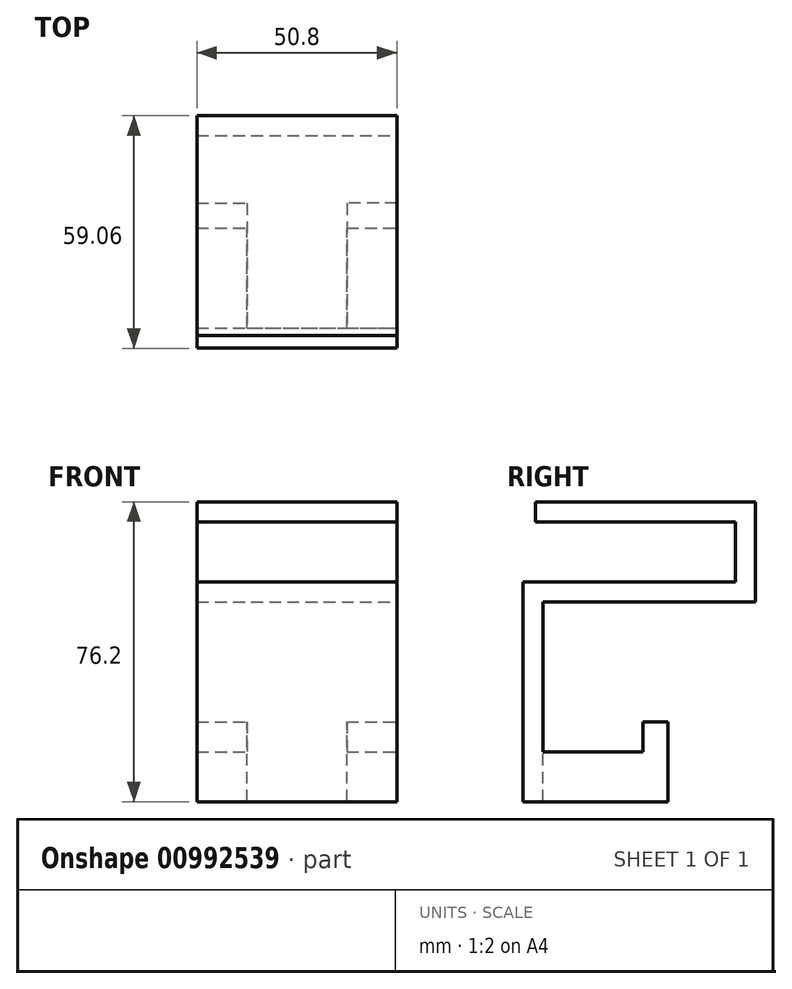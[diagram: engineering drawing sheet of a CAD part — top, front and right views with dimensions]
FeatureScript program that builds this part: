
annotation { "Feature Type Name" : "Feature", "Feature Type Description" : "" }
export const myFeature = defineFeature(function(context is Context, id is Id, definition is map)
    precondition{}
    {
        {
            var Q0;
            Q0=qCreatedBy(makeId("Top.planeOp"),FACE);
            var sketch = newSketch(context, id + "F0", { "sketchPlane" : qUnion([Q0])});
            skLineSegment(sketch, "E0.bottom", {"start": v(0, 0) * mm, "end": v(50.8, 0) * mm});
            skLineSegment(sketch, "E0.top", {"start": v(0, 55.88) * mm, "end": v(50.8, 55.88) * mm});
            skLineSegment(sketch, "E0.left", {"start": v(0, 0) * mm, "end": v(0, 55.88) * mm});
            skLineSegment(sketch, "E0.right", {"start": v(50.8, 0) * mm, "end": v(50.8, 55.88) * mm});
            skSolve(sketch);
        }
        {
            var Q0;
            Q0=makeQuery(id+"F0.imprint","IMPRINT",FACE,{"disambiguationData":[TD([[makeQuery(id+"F0.imprint","IMPRINT",EDGE,{"derivedFrom":sQuery(id+"F0.wireOp",EDGE,"E0.bottom")}),1.0]])]});
            extrude(context, id + "F1", {"entities" : qUnion([Q0]), "depth" : 5.08 * mm, "offsetDistance" : 25.4 * mm});
        }
        {
            var Q0;
            Q0=makeQuery(id+"F1.opExtrude","CAP_FACE",FACE,{"disambiguationData":[OSD([sQuery(id+"F0.wireOp",EDGE,"E0.bottom"),sQuery(id+"F0.wireOp",EDGE,"E0.top"),sQuery(id+"F0.wireOp",EDGE,"E0.left"),sQuery(id+"F0.wireOp",EDGE,"E0.right")])],"isStart":true});
            var sketch = newSketch(context, id + "F2", { "sketchPlane" : qUnion([Q0])});
            skLineSegment(sketch, "E1.bottom", {"start": v(0, -55.88) * mm, "end": v(50.8, -55.88) * mm});
            skLineSegment(sketch, "E1.top", {"start": v(0, -50.8) * mm, "end": v(50.8, -50.8) * mm});
            skLineSegment(sketch, "E1.left", {"start": v(0, -55.88) * mm, "end": v(0, -50.8) * mm});
            skLineSegment(sketch, "E1.right", {"start": v(50.8, -55.88) * mm, "end": v(50.8, -50.8) * mm});
            skSolve(sketch);
        }
        {
            var Q0;
            Q0=makeQuery(id+"F2.imprint","IMPRINT",FACE,{"disambiguationData":[TD([[makeQuery(id+"F2.imprint","IMPRINT",EDGE,{"derivedFrom":sQuery(id+"F2.wireOp",EDGE,"E1.bottom")}),1.0]])]});
            extrude(context, id + "F3", {"entities" : qUnion([Q0]), "operationType" : NewBodyOperationType.ADD, "depth" : 20.32 * mm, "offsetDistance" : 25.4 * mm});
        }
        {
            var Q0;
            Q0=makeQuery(id+"F3.opExtrude","SWEPT_FACE",FACE,{"disambiguationData":[OSD([sQuery(id+"F2.wireOp",EDGE,"E1.top")])]});
            var sketch = newSketch(context, id + "F4", { "sketchPlane" : qUnion([Q0])});
            skLineSegment(sketch, "E2.bottom", {"start": v(0, -20.32) * mm, "end": v(50.8, -20.32) * mm});
            skLineSegment(sketch, "E2.top", {"start": v(0, -15.24) * mm, "end": v(50.8, -15.24) * mm});
            skLineSegment(sketch, "E2.left", {"start": v(0, -20.32) * mm, "end": v(0, -15.24) * mm});
            skLineSegment(sketch, "E2.right", {"start": v(50.8, -20.32) * mm, "end": v(50.8, -15.24) * mm});
            skSolve(sketch);
        }
        {
            var Q0;
            Q0=makeQuery(id+"F4.imprint","IMPRINT",FACE,{"disambiguationData":[TD([[makeQuery(id+"F4.imprint","IMPRINT",EDGE,{"derivedFrom":sQuery(id+"F4.wireOp",EDGE,"E2.bottom")}),1.0]])]});
            extrude(context, id + "F5", {"entities" : qUnion([Q0]), "operationType" : NewBodyOperationType.ADD, "depth" : 53.97 * mm, "offsetDistance" : 25.4 * mm});
        }
        {
            var Q0;
            Q0=makeQuery(id+"F5.boolean.opBoolean","MERGE",FACE,{"derivedFrom":[makeQuery(id+"F3.opExtrude","CAP_FACE",FACE,{"disambiguationData":[OSD([sQuery(id+"F2.wireOp",EDGE,"E1.bottom"),sQuery(id+"F2.wireOp",EDGE,"E1.top"),sQuery(id+"F2.wireOp",EDGE,"E1.left"),sQuery(id+"F2.wireOp",EDGE,"E1.right")])],"isStart":false}),makeQuery(id+"F5.opExtrude","SWEPT_FACE",FACE,{"disambiguationData":[OSD([sQuery(id+"F4.wireOp",EDGE,"E2.bottom")])]})]});
            var sketch = newSketch(context, id + "F6", { "sketchPlane" : qUnion([Q0])});
            skLineSegment(sketch, "E3.bottom", {"start": v(0, 3.17) * mm, "end": v(50.8, 3.17) * mm});
            skLineSegment(sketch, "E3.top", {"start": v(0, -1.9) * mm, "end": v(50.8, -1.9) * mm});
            skLineSegment(sketch, "E3.left", {"start": v(0, 3.17) * mm, "end": v(0, -1.9) * mm});
            skLineSegment(sketch, "E3.right", {"start": v(50.8, 3.17) * mm, "end": v(50.8, -1.9) * mm});
            skSolve(sketch);
        }
        {
            var Q0;
            Q0=makeQuery(id+"F6.imprint","IMPRINT",FACE,{"disambiguationData":[TD([[makeQuery(id+"F6.imprint","IMPRINT",EDGE,{"derivedFrom":sQuery(id+"F6.wireOp",EDGE,"E3.bottom")}),-1.0]])]});
            extrude(context, id + "F7", {"entities" : qUnion([Q0]), "operationType" : NewBodyOperationType.ADD, "depth" : 50.8 * mm, "offsetDistance" : 25.4 * mm});
        }
        {
            var Q0;
            Q0=makeQuery(id+"F7.opExtrude","SWEPT_FACE",FACE,{"disambiguationData":[OSD([sQuery(id+"F6.wireOp",EDGE,"E3.top")])]});
            var sketch = newSketch(context, id + "F8", { "sketchPlane" : qUnion([Q0])});
            skLineSegment(sketch, "E4.bottom", {"start": v(-50.8, -71.12) * mm, "end": v(-38.1, -71.12) * mm});
            skLineSegment(sketch, "E4.top", {"start": v(-50.8, -50.8) * mm, "end": v(-38.1, -50.8) * mm});
            skLineSegment(sketch, "E4.left", {"start": v(-50.8, -71.12) * mm, "end": v(-50.8, -50.8) * mm});
            skLineSegment(sketch, "E4.right", {"start": v(-38.1, -71.12) * mm, "end": v(-38.1, -50.8) * mm});
            skLineSegment(sketch, "E5.bottom", {"start": v(0, -71.12) * mm, "end": v(-12.7, -71.12) * mm});
            skLineSegment(sketch, "E5.top", {"start": v(0, -50.8) * mm, "end": v(-12.7, -50.8) * mm});
            skLineSegment(sketch, "E5.left", {"start": v(0, -71.12) * mm, "end": v(0, -50.8) * mm});
            skLineSegment(sketch, "E5.right", {"start": v(-12.7, -71.12) * mm, "end": v(-12.7, -50.8) * mm});
            skSolve(sketch);
        }
        {
            var Q0;
            Q0=makeQuery(id+"F8.imprint","IMPRINT",FACE,{"disambiguationData":[TD([[makeQuery(id+"F8.imprint","IMPRINT",EDGE,{"derivedFrom":sQuery(id+"F8.wireOp",EDGE,"E4.bottom")}),-1.0]])]});
            var Q1;
            Q1=makeQuery(id+"F8.imprint","IMPRINT",FACE,{"disambiguationData":[TD([[makeQuery(id+"F8.imprint","IMPRINT",EDGE,{"derivedFrom":sQuery(id+"F8.wireOp",EDGE,"E5.bottom")}),-1.0]])]});
            extrude(context, id + "F9", {"entities" : qUnion([Q0, Q1]), "operationType" : NewBodyOperationType.ADD, "depth" : 31.75 * mm, "offsetDistance" : 25.4 * mm});
        }
        {
            var Q0;
            Q0=makeQuery(id+"F9.boolean.opBoolean","MERGE",FACE,{"derivedFrom":[makeQuery(id+"F7.boolean.opBoolean","MERGE",FACE,{"derivedFrom":[makeQuery(id+"F5.boolean.opBoolean","MERGE",FACE,{"derivedFrom":[makeQuery(id+"F3.boolean.opBoolean","MERGE",FACE,{"derivedFrom":[makeQuery(id+"F1.opExtrude","SWEPT_FACE",FACE,{"disambiguationData":[OSD([sQuery(id+"F0.wireOp",EDGE,"E0.right")])]}),makeQuery(id+"F3.opExtrude","SWEPT_FACE",FACE,{"disambiguationData":[OSD([sQuery(id+"F2.wireOp",EDGE,"E1.right")])]})]}),makeQuery(id+"F5.opExtrude","SWEPT_FACE",FACE,{"disambiguationData":[OSD([sQuery(id+"F4.wireOp",EDGE,"E2.right")])]})]}),makeQuery(id+"F7.opExtrude","SWEPT_FACE",FACE,{"disambiguationData":[OSD([sQuery(id+"F6.wireOp",EDGE,"E3.right")])]})]}),makeQuery(id+"F9.opExtrude","SWEPT_FACE",FACE,{"disambiguationData":[OSD([sQuery(id+"F8.wireOp",EDGE,"E4.left")])]})]});
            var sketch = newSketch(context, id + "F10", { "sketchPlane" : qUnion([Q0])});
            skLineSegment(sketch, "E6.bottom", {"start": v(1.9, -50.8) * mm, "end": v(27.3, -50.8) * mm});
            skLineSegment(sketch, "E6.top", {"start": v(1.9, -58.42) * mm, "end": v(27.3, -58.42) * mm});
            skLineSegment(sketch, "E6.left", {"start": v(1.9, -50.8) * mm, "end": v(1.9, -58.42) * mm});
            skLineSegment(sketch, "E6.right", {"start": v(27.3, -50.8) * mm, "end": v(27.3, -58.42) * mm});
            skSolve(sketch);
        }
        {
            var Q0;
            Q0=makeQuery(id+"F10.imprint","IMPRINT",FACE,{"disambiguationData":[TD([[makeQuery(id+"F10.imprint","IMPRINT",EDGE,{"derivedFrom":sQuery(id+"F10.wireOp",EDGE,"E6.bottom")}),1.0]])]});
            extrude(context, id + "F11", {"entities" : qUnion([Q0]), "operationType" : NewBodyOperationType.REMOVE, "oppositeDirection" : true, "depth" : 50.8 * mm, "offsetDistance" : 25.4 * mm});
        }
    });
